# Revit family: KingswayGroup_ShrLcksAndStrkPlts_SwingThruStrikePlate
name_source: partatom
category: Specialty Equipment
units: mm (PartAtom-declared; Revit-internal decimal feet)

## family parameters
Always vertical = Yes
Cut with Voids When Loaded = No
Part Type = Normal
Room Calculation Point = No
Round Connector Dimension = Use Diameter
Shared = No
Work Plane-Based = No

## types (1)
- KingswayGroup_ShrLcksAndStrkPlts_SwingThruStrikePlate
    AssetType = Fixed
    BIMObjectName = KingswayGroup_ShearLocksAndStrikePlates_SwingThruStrikePlate
    Category = Pr_75_30_27_77:Shear locks and strike plates
    Color = For full range of available finishes and colours, contact Kingsway Group
    Default Elevation = 0 mm  [stored 0 ft]
    Description = SwingThru Double Action Strike Plate
    DurationUnit = year
    Features = The SwingThru Strike Plate is a key component of the SWING Anti-Barricade Door System that allows the door leaf to open outwards without needing to retract the lock bolt. This system is the simplest and most effective means of overcoming barricade situations.
    Finish = For full range of available finishes and colours, contact Kingsway Group
    IfcExportAs = IfcDiscreteAccessoryType
    IfcExportType = USERDEFINED
    Manufacturer = Kingsway Group
    ManufacturerName = Kingsway Group
    ManufacturerURL = https://kingswaygroupglobal.com
    Material = For full range of available material, contact Kingsway Group
    Model = KG149
    ModelNumber = KG149
    ModelReference = SwingThru Strike Plate
    Name = ShearLocksAndStrikePlates_SwingThruStrikePlate_KG149_KingswayGroup
    NominalHeight = 200 mm  [stored 0.656168 ft]
    NominalLength = 140 mm  [stored 0.459318 ft]
    NominalWidth = 18 mm  [stored 0.0590551 ft]
    ProductInformation = https://kingswaygroupglobal.com
    Size = 140 x 200 x 18
    URL = https://kingswaygroupglobal.com
    Uniclass2015Code = Pr_75_30_27_77
    Uniclass2015Title = Shear locks and strike plates
    Uniclass2015Version = Products v1.36
    Version = 1
    WarrantyDescription = 5-Year Guarantee *For faulty manufacture and not for damage
    WarrantyDurationParts = 5
    WarrantyDurationUnit = year

note: [stored X ft] marks values corroborated as IEEE doubles in the binary element streams (Revit-internal decimal feet)

## geometry (parser evidence)
native form markers: Sweep x2
no freeform markers — native parametric forms only
